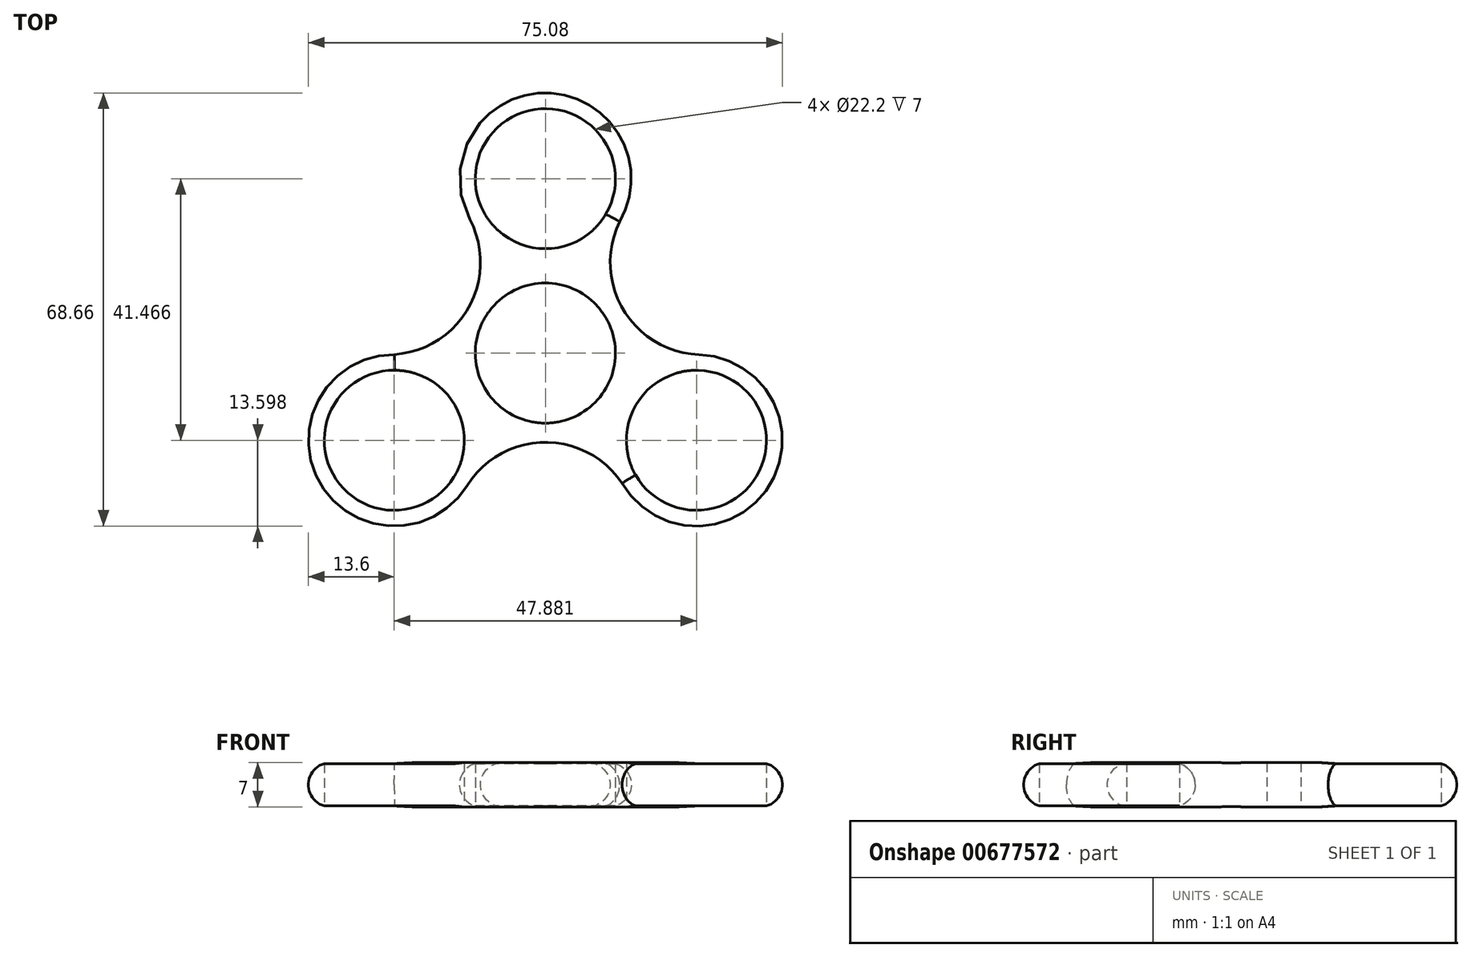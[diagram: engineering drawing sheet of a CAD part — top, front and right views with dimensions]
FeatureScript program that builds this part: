
annotation { "Feature Type Name" : "Feature", "Feature Type Description" : "" }
export const myFeature = defineFeature(function(context is Context, id is Id, definition is map)
    precondition{}
    {
        {
            var Q0;
            Q0=qCreatedBy(makeId("Top.planeOp"),FACE);
            var sketch = newSketch(context, id + "F0", { "sketchPlane" : qUnion([Q0])});
            skCircle(sketch, "E0", {"center": v(0, 0) * mm, "radius": 11.1 * mm});
            skCircle(sketch, "E1", {"center": v(0, 27.64) * mm, "radius": 11.1 * mm});
            skArc(sketch, "E2", {"start": v(11.78, 20.84) * mm, "mid": v(0.2, 41.24) * mm, "end": v(-11.97, 21.19) * mm});
            skCircle(sketch, "E3.1.0", {"center": v(-23.94, -13.82) * mm, "radius": 11.1 * mm});
            skArc(sketch, "E3.1.1", {"start": v(-23.94, -0.22) * mm, "mid": v(-35.82, -20.45) * mm, "end": v(-12.36, -20.96) * mm});
            skCircle(sketch, "E3.2.0", {"center": v(23.94, -13.82) * mm, "radius": 11.1 * mm});
            skArc(sketch, "E3.2.1", {"start": v(12.16, -20.62) * mm, "mid": v(35.62, -20.8) * mm, "end": v(24.33, -0.23) * mm});
            skArc(sketch, "E4", {"start": v(-23.94, -0.22) * mm, "mid": v(-12.15, 7.23) * mm, "end": v(-11.97, 21.19) * mm});
            skPoint(sketch, "E4.startSnap0", {"position": v(-23.94, 0) * mm});
            skPoint(sketch, "E4.endSnap0", {"position": v(-11.97, 20.73) * mm});
            skArc(sketch, "E5.1.0", {"start": v(12.16, -20.62) * mm, "mid": v(-0.2, -14.14) * mm, "end": v(-12.36, -20.96) * mm});
            skArc(sketch, "E5.2.0", {"start": v(11.78, 20.84) * mm, "mid": v(12.34, 6.9) * mm, "end": v(24.33, -0.23) * mm});
            skSolve(sketch);
        }
        {
            var Q0;
            Q0 = qSketchRegion(id + "F0", true);
            extrude(context, id + "F1", {"entities" : qUnion([Q0]), "depth" : 7 * mm, "offsetDistance" : 25 * mm});
        }
        {
            var Q0;
            Q0=makeQuery(id+"F1.opExtrude","CAP_EDGE",EDGE,{"disambiguationData":[OSD([sQuery(id+"F0.wireOp",EDGE,"E3.1.1")])],"isStart":false});
            var Q1;
            Q1=makeQuery(id+"F1.opExtrude","CAP_EDGE",EDGE,{"disambiguationData":[OSD([sQuery(id+"F0.wireOp",EDGE,"E4")])],"isStart":false});
            var Q2;
            Q2=makeQuery(id+"F1.opExtrude","CAP_EDGE",EDGE,{"disambiguationData":[OSD([sQuery(id+"F0.wireOp",EDGE,"E5.1.0")])],"isStart":false});
            var Q3;
            Q3=makeQuery(id+"F1.opExtrude","CAP_EDGE",EDGE,{"disambiguationData":[OSD([sQuery(id+"F0.wireOp",EDGE,"E2")])],"isStart":false});
            var Q4;
            Q4=makeQuery(id+"F1.opExtrude","CAP_EDGE",EDGE,{"disambiguationData":[OSD([sQuery(id+"F0.wireOp",EDGE,"E5.2.0")])],"isStart":false});
            var Q5;
            Q5=makeQuery(id+"F1.opExtrude","CAP_EDGE",EDGE,{"disambiguationData":[OSD([sQuery(id+"F0.wireOp",EDGE,"E3.2.1")])],"isStart":false});
            var Q6;
            Q6=makeQuery(id+"F1.opExtrude","CAP_EDGE",EDGE,{"disambiguationData":[OSD([sQuery(id+"F0.wireOp",EDGE,"E4")])],"isStart":true});
            var Q7;
            Q7=makeQuery(id+"F1.opExtrude","CAP_EDGE",EDGE,{"disambiguationData":[OSD([sQuery(id+"F0.wireOp",EDGE,"E2")])],"isStart":true});
            var Q8;
            Q8=makeQuery(id+"F1.opExtrude","CAP_EDGE",EDGE,{"disambiguationData":[OSD([sQuery(id+"F0.wireOp",EDGE,"E5.2.0")])],"isStart":true});
            var Q9;
            Q9=makeQuery(id+"F1.opExtrude","CAP_EDGE",EDGE,{"disambiguationData":[OSD([sQuery(id+"F0.wireOp",EDGE,"E3.2.1")])],"isStart":true});
            var Q10;
            Q10=makeQuery(id+"F1.opExtrude","CAP_EDGE",EDGE,{"disambiguationData":[OSD([sQuery(id+"F0.wireOp",EDGE,"E5.1.0")])],"isStart":true});
            var Q11;
            Q11=makeQuery(id+"F1.opExtrude","CAP_EDGE",EDGE,{"disambiguationData":[OSD([sQuery(id+"F0.wireOp",EDGE,"E3.1.1")])],"isStart":true});
            fillet(context, id + "F2", {"entities" : qUnion([Q0, Q1, Q2, Q3, Q4, Q5, Q6, Q7, Q8, Q9, Q10, Q11]), "radius" : 3.5 * mm, "tangentPropagation" : true, "allowEdgeOverflow" : false});
        }
    });
